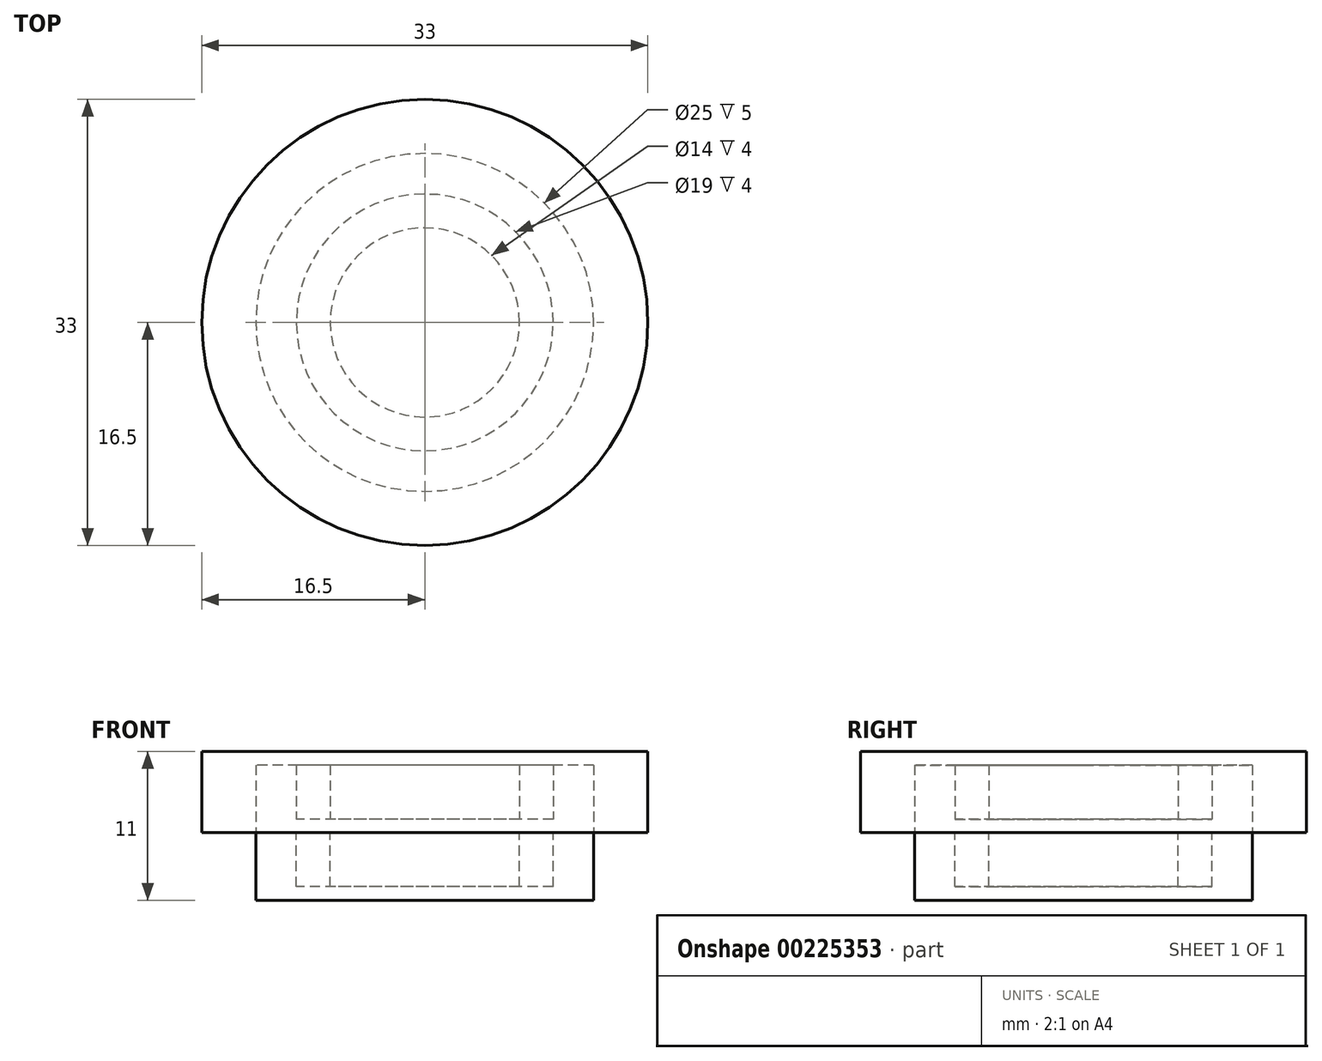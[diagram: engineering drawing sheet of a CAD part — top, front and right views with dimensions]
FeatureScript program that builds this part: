
annotation { "Feature Type Name" : "Feature", "Feature Type Description" : "" }
export const myFeature = defineFeature(function(context is Context, id is Id, definition is map)
    precondition{}
    {
        {
            var Q0;
            Q0=qCreatedBy(makeId("Top.planeOp"),FACE);
            var sketch = newSketch(context, id + "F0", { "sketchPlane" : qUnion([Q0])});
            skCircle(sketch, "E0", {"center": v(0, 0) * mm, "radius": 12.5 * mm});
            skSolve(sketch);
        }
        {
            var Q0;
            Q0=makeQuery(id+"F0.imprint","IMPRINT",FACE,{"disambiguationData":[TD([[makeQuery(id+"F0.imprint","IMPRINT",EDGE,{"derivedFrom":sQuery(id+"F0.wireOp",EDGE,"E0")}),1.0]])]});
            var Q1;
            Q1=sQuery(id+"F0.wireOp",EDGE,"E0");
            extrude(context, id + "F1", {"entities" : qUnion([Q0]), "surfaceEntities" : qUnion([Q1]), "depth" : 5 * mm});
        }
        {
            var Q0;
            Q0=makeQuery(id+"F1.opExtrude","CAP_FACE",FACE,{"disambiguationData":[OSD([sQuery(id+"F0.wireOp",EDGE,"E0")])],"isStart":false});
            var sketch = newSketch(context, id + "F2", { "sketchPlane" : qUnion([Q0])});
            skCircle(sketch, "E1", {"center": v(0, 0) * mm, "radius": 9.5 * mm});
            skCircle(sketch, "E2", {"center": v(0, 0) * mm, "radius": 7 * mm});
            skSolve(sketch);
        }
        {
            var Q0;
            Q0=makeQuery(id+"F2.imprint","IMPRINT",FACE,{"disambiguationData":[TD([[makeQuery(id+"F2.imprint","IMPRINT",EDGE,{"derivedFrom":sQuery(id+"F2.wireOp",EDGE,"E1")}),1.0]])]});
            var Q1;
            Q1=sQuery(id+"F2.wireOp",EDGE,"E2");
            var Q2;
            Q2=sQuery(id+"F2.wireOp",EDGE,"E1");
            extrude(context, id + "F3", {"entities" : qUnion([Q0]), "operationType" : NewBodyOperationType.REMOVE, "surfaceEntities" : qUnion([Q1, Q2]), "oppositeDirection" : true, "depth" : 4 * mm});
        }
        {
            var Q0;
            {var subQ0=sQuery(id+"F0.wireOp",EDGE,"E0");Q0=makeQuery(id+"F3.boolean.opBoolean","SPLIT",FACE,{"disambiguationData":[TD([makeQuery(id+"F1.opExtrude","SWEPT_FACE",FACE,{"disambiguationData":[OSD([subQ0])]})])],"derivedFrom":makeQuery(id+"F1.opExtrude","CAP_FACE",FACE,{"disambiguationData":[OSD([subQ0])],"isStart":false})});}
            var sketch = newSketch(context, id + "F4", { "sketchPlane" : qUnion([Q0])});
            skCircle(sketch, "E3.0", {"center": v(0, 0) * mm, "radius": 12.5 * mm});
            skCircle(sketch, "E4.0", {"center": v(0, 0) * mm, "radius": 7 * mm});
            skCircle(sketch, "E5.0", {"center": v(0, 0) * mm, "radius": 9.5 * mm});
            skCircle(sketch, "E6", {"center": v(0, 0) * mm, "radius": 16.5 * mm});
            skSolve(sketch);
        }
        {
            var Q0;
            Q0=makeQuery(id+"F4.imprint","IMPRINT",FACE,{"disambiguationData":[TD([[makeQuery(id+"F4.imprint","IMPRINT",EDGE,{"derivedFrom":sQuery(id+"F4.wireOp",EDGE,"E3.0")}),-1.0]])]});
            var Q1;
            Q1=makeQuery(id+"F4.imprint","IMPRINT",FACE,{"disambiguationData":[TD([[makeQuery(id+"F4.imprint","IMPRINT",EDGE,{"derivedFrom":sQuery(id+"F4.wireOp",EDGE,"E4.0")}),-1.0]])]});
            var Q2;
            Q2=makeQuery(id+"F4.imprint","IMPRINT",FACE,{"disambiguationData":[TD([[makeQuery(id+"F4.imprint","IMPRINT",EDGE,{"derivedFrom":sQuery(id+"F4.wireOp",EDGE,"E4.0")}),1.0]])]});
            var Q3;
            Q3=makeQuery(id+"F4.imprint","IMPRINT",FACE,{"disambiguationData":[TD([[makeQuery(id+"F4.imprint","IMPRINT",EDGE,{"derivedFrom":sQuery(id+"F4.wireOp",EDGE,"E3.0")}),1.0]])]});
            var Q4;
            Q4=sQuery(id+"F4.wireOp",EDGE,"E6");
            extrude(context, id + "F5", {"entities" : qUnion([Q0, Q1, Q2, Q3]), "surfaceEntities" : qUnion([Q4]), "depth" : 6 * mm});
        }
        {
            var Q0;
            Q0=makeQuery(id+"F4.imprint","IMPRINT",FACE,{"disambiguationData":[TD([[makeQuery(id+"F4.imprint","IMPRINT",EDGE,{"derivedFrom":sQuery(id+"F4.wireOp",EDGE,"E4.0")}),1.0]])]});
            var Q1;
            Q1=makeQuery(id+"F4.imprint","IMPRINT",FACE,{"disambiguationData":[TD([[makeQuery(id+"F4.imprint","IMPRINT",EDGE,{"derivedFrom":sQuery(id+"F4.wireOp",EDGE,"E3.0")}),1.0]])]});
            extrude(context, id + "F6", {"entities" : qUnion([Q0, Q1]), "operationType" : NewBodyOperationType.REMOVE, "depth" : 5 * mm});
        }
        {
            var Q0;
            Q0=makeQuery(id+"F4.imprint","IMPRINT",FACE,{"disambiguationData":[TD([[makeQuery(id+"F4.imprint","IMPRINT",EDGE,{"derivedFrom":sQuery(id+"F4.wireOp",EDGE,"E4.0")}),-1.0]])]});
            var sketch = newSketch(context, id + "F7", { "sketchPlane" : qUnion([Q0])});
            skCircle(sketch, "E7.0", {"center": v(0, 0) * mm, "radius": 9.5 * mm});
            skSolve(sketch);
        }
        {
            var Q0;
            Q0 = qSketchRegion(id + "F7", true);
            extrude(context, id + "F8", {"entities" : qUnion([Q0]), "operationType" : NewBodyOperationType.REMOVE, "depth" : 1 * mm});
        }
    });
